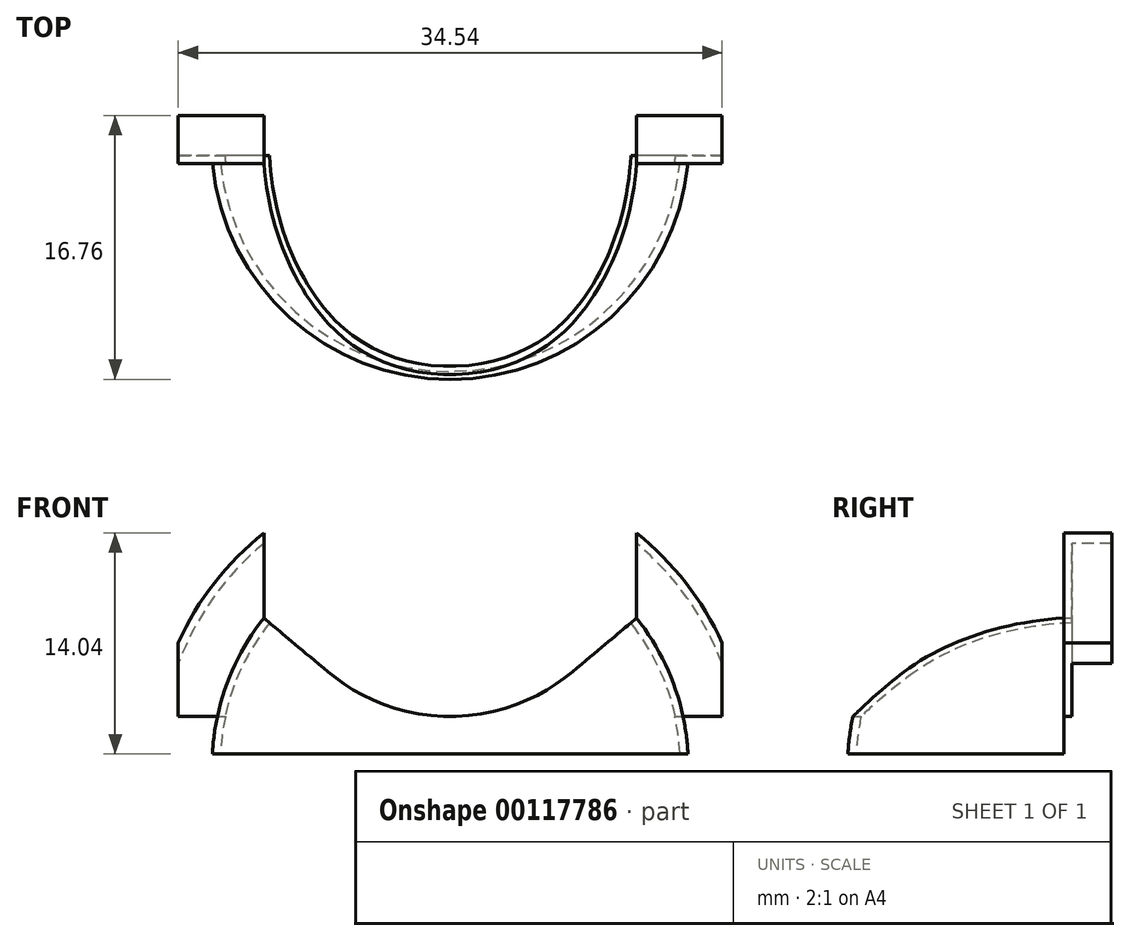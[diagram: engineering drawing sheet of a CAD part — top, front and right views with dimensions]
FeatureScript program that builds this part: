
annotation { "Feature Type Name" : "Feature", "Feature Type Description" : "" }
export const myFeature = defineFeature(function(context is Context, id is Id, definition is map)
    precondition{}
    {
        {
            var Q0;
            Q0=qCreatedBy(makeId("Right.planeOp"),FACE);
            var sketch = newSketch(context, id + "F0", { "sketchPlane" : qUnion([Q0])});
            skCircle(sketch, "E0", {"center": v(0, 0) * mm, "radius": 14.69 * mm});
            skLineSegment(sketch, "E1", {"start": v(1.59, 18.47) * mm, "end": v(-0.95, 18.47) * mm});
            skLineSegment(sketch, "E2", {"start": v(-0.95, 18.47) * mm, "end": v(-0.95, 14.66) * mm});
            skLineSegment(sketch, "E3", {"start": v(1.59, 18.47) * mm, "end": v(1.59, 18.97) * mm});
            skLineSegment(sketch, "E4", {"start": v(1.59, 18.97) * mm, "end": v(-1.46, 18.97) * mm});
            skLineSegment(sketch, "E5", {"start": v(-1.46, 18.97) * mm, "end": v(-1.46, 15.12) * mm});
            skCircle(sketch, "E6", {"center": v(0, 0) * mm, "radius": 15.2 * mm});
            skLineSegment(sketch, "E7", {"start": v(-15.2, 0) * mm, "end": v(-14.69, 0) * mm});
            skSolve(sketch);
        }
        {
            var Q0;
            {var subQ1=sQuery(id+"F0.wireOp",EDGE,"E1");Q0=makeQuery(id+"F0.imprint","IMPRINT",FACE,{"disambiguationData":[TD([[makeQuery(id+"F0.imprint","IMPRINT",EDGE,{"derivedFrom":subQ1}),-1.0]])]});}
            var Q1;
            {var subQ6=sQuery(id+"F0.wireOp",EDGE,"E7");Q1=makeQuery(id+"F0.imprint","IMPRINT",FACE,{"disambiguationData":[TD([[makeQuery(id+"F0.imprint","IMPRINT",EDGE,{"derivedFrom":subQ6}),1.0]])]});}
            var Q2;
            Q2=sQuery(id+"F0.wireOp",EDGE,"E7");
            revolve(context, id + "F1", {"entities" : qUnion([Q0, Q1]), "axis" : qUnion([Q2]), "revolveType" : RevolveType.SYMMETRIC, "angle" : 180 * degree});
        }
        {
            var Q0;
            Q0=qCreatedBy(makeId("Right.planeOp"),FACE);
            var sketch = newSketch(context, id + "F2", { "sketchPlane" : qUnion([Q0])});
            skLineSegment(sketch, "E8.bottom", {"start": v(1.59, 3.17) * mm, "end": v(-1.46, 3.17) * mm});
            skLineSegment(sketch, "E8.top", {"start": v(1.59, 0) * mm, "end": v(-1.46, 0) * mm});
            skLineSegment(sketch, "E8.left", {"start": v(1.59, 3.17) * mm, "end": v(1.59, 0) * mm});
            skLineSegment(sketch, "E8.right", {"start": v(-1.46, 3.17) * mm, "end": v(-1.46, 0) * mm});
            skSolve(sketch);
        }
        {
            var Q0;
            Q0=makeQuery(id+"F2.imprint","IMPRINT",FACE,{"disambiguationData":[TD([[makeQuery(id+"F2.imprint","IMPRINT",EDGE,{"derivedFrom":sQuery(id+"F2.wireOp",EDGE,"E8.bottom")}),1.0]])]});
            extrude(context, id + "F3", {"entities" : qUnion([Q0]), "operationType" : NewBodyOperationType.REMOVE, "endBound" : BoundingType.SYMMETRIC, "oppositeDirection" : true, "depth" : 50.8 * mm});
        }
        {
            var Q0;
            Q0=makeQuery(id+"F1.opRevolve","SWEPT_BODY",BODY,{"disambiguationData":[OSD([sQuery(id+"F0.wireOp",EDGE,"E0"),sQuery(id+"F0.wireOp",EDGE,"E1"),sQuery(id+"F0.wireOp",EDGE,"E2"),sQuery(id+"F0.wireOp",EDGE,"E3"),sQuery(id+"F0.wireOp",EDGE,"E4"),sQuery(id+"F0.wireOp",EDGE,"E5"),sQuery(id+"F0.wireOp",EDGE,"E6"),sQuery(id+"F0.wireOp",EDGE,"E7")])]});
            var Q1;
            Q1=makeQuery(id+"F3.boolean.opBoolean","COPY",EDGE,{"disambiguationData":[OD(1.0)],"derivedFrom":makeQuery(id+"F3.opExtrude","SWEPT_EDGE",EDGE,{"disambiguationData":[OSD([sQuery(id+"F2.wireOp",EDGE,"E8.top"),sQuery(id+"F2.wireOp",EDGE,"E8.right")])]})});
            transform(context, id + "F4", {"entities" : qUnion([Q0]), "transformType" : TransformType.COPY});
        }
        {
            var Q0;
            Q0=qCreatedBy(makeId("Front.planeOp"),FACE);
            var sketch = newSketch(context, id + "F5", { "sketchPlane" : qUnion([Q0])});
            skCircle(sketch, "E9", {"center": v(0, 15.24) * mm, "radius": 12.07 * mm});
            skLineSegment(sketch, "E10", {"start": v(11.83, 9.42) * mm, "end": v(7.76, 6) * mm});
            skLineSegment(sketch, "E11", {"start": v(-7.76, 6) * mm, "end": v(-11.83, 9.42) * mm});
            skLineSegment(sketch, "E12", {"start": v(-11.83, 9.42) * mm, "end": v(11.83, 9.42) * mm});
            skLineSegment(sketch, "E13", {"start": v(-11.83, 9.42) * mm, "end": v(-11.83, 20.56) * mm});
            skLineSegment(sketch, "E14", {"start": v(-11.83, 20.56) * mm, "end": v(11.83, 20.56) * mm});
            skLineSegment(sketch, "E15", {"start": v(11.83, 20.56) * mm, "end": v(11.83, 9.42) * mm});
            skSolve(sketch);
        }
        {
            var Q0;
            {var subQ0=sQuery(id+"F5.wireOp",EDGE,"1CEebHZN-BrZE-F3CF-ijxN-NzDrlZ3mt1Ko.top");Q0=makeQuery(id+"F5.imprint","IMPRINT",FACE,{"disambiguationData":[TD([[makeQuery(id+"F5.imprint","IMPRINT",EDGE,{"derivedFrom":subQ0}),-1.0]])]});}
            var Q1;
            {var subQ0=sQuery(id+"F5.wireOp",EDGE,"1CEebHZN-BrZE-F3CF-ijxN-NzDrlZ3mt1Ko.top");Q1=makeQuery(id+"F5.imprint","IMPRINT",FACE,{"disambiguationData":[TD([[makeQuery(id+"F5.imprint","IMPRINT",EDGE,{"derivedFrom":subQ0}),1.0]])]});}
            var Q2;
            Q2=makeQuery(id+"F5.imprint","IMPRINT",FACE,{"disambiguationData":[TD([[makeQuery(id+"F5.imprint","IMPRINT",EDGE,{"derivedFrom":sQuery(id+"F5.wireOp",EDGE,"1CEebHZN-BrZE-F3CF-ijxN-NzDrlZ3mt1Ko.bottom")}),-1.0]])]});
            var Q3;
            {var subQ1=sQuery(id+"F5.wireOp",EDGE,"E10");Q3=makeQuery(id+"F5.imprint","IMPRINT",FACE,{"disambiguationData":[TD([[makeQuery(id+"F5.imprint","IMPRINT",EDGE,{"derivedFrom":subQ1}),-1.0]])]});}
            var Q4;
            {var subQ0=sQuery(id+"F5.wireOp",EDGE,"E9");var subQ1=makeQuery(id+"F5.imprint","INTERSECT",VERTEX,{"derivedFrom":[subQ0,sQuery(id+"F5.wireOp",EDGE,"E10")]});Q4=makeQuery(id+"F5.imprint","IMPRINT",FACE,{"disambiguationData":[TD([[makeQuery(id+"F5.imprint","IMPRINT",EDGE,{"disambiguationData":[TD([[subQ1,1.0]])],"derivedFrom":subQ0}),1.0]])]});}
            var Q5;
            {var subQ0=sQuery(id+"F5.wireOp",EDGE,"E13");Q5=makeQuery(id+"F5.imprint","IMPRINT",FACE,{"disambiguationData":[TD([[makeQuery(id+"F5.imprint","IMPRINT",EDGE,{"derivedFrom":subQ0}),-1.0]])]});}
            var Q6;
            {var subQ0=sQuery(id+"F5.wireOp",EDGE,"E12");var subQ1=sQuery(id+"F5.wireOp",EDGE,"E9");var subQ2=makeQuery(id+"F5.imprint","INTERSECT",VERTEX,{"disambiguationData":[OD(0.0)],"derivedFrom":[subQ1,subQ0]});Q6=makeQuery(id+"F5.imprint","IMPRINT",FACE,{"disambiguationData":[TD([[makeQuery(id+"F5.imprint","IMPRINT",EDGE,{"disambiguationData":[TD([[subQ2,1.0]])],"derivedFrom":subQ1}),1.0]])]});}
            var Q7;
            {var subQ0=sQuery(id+"F5.wireOp",EDGE,"E11");Q7=makeQuery(id+"F5.imprint","IMPRINT",FACE,{"disambiguationData":[TD([[makeQuery(id+"F5.imprint","IMPRINT",EDGE,{"derivedFrom":subQ0}),-1.0]])]});}
            var Q8;
            {var subQ5=sQuery(id+"F5.wireOp",EDGE,"E15");Q8=makeQuery(id+"F5.imprint","IMPRINT",FACE,{"disambiguationData":[TD([[makeQuery(id+"F5.imprint","IMPRINT",EDGE,{"derivedFrom":subQ5}),-1.0]])]});}
            extrude(context, id + "F6", {"entities" : qUnion([Q0, Q1, Q2, Q3, Q4, Q5, Q6, Q7, Q8]), "operationType" : NewBodyOperationType.REMOVE, "endBound" : BoundingType.SYMMETRIC, "depth" : 50.8 * mm});
        }
        {
            var Q0;
            Q0=qCreatedBy(makeId("Front.planeOp"),FACE);
            var sketch = newSketch(context, id + "F7", { "sketchPlane" : qUnion([Q0])});
            skLineSegment(sketch, "E16.bottom", {"start": v(-17.27, 0) * mm, "end": v(-29.97, 0) * mm});
            skLineSegment(sketch, "E16.top", {"start": v(-17.27, 12.7) * mm, "end": v(-29.97, 12.7) * mm});
            skLineSegment(sketch, "E16.left", {"start": v(-17.27, 0) * mm, "end": v(-17.27, 12.7) * mm});
            skLineSegment(sketch, "E16.right", {"start": v(-29.97, 0) * mm, "end": v(-29.97, 12.7) * mm});
            skLineSegment(sketch, "E17.bottom", {"start": v(17.27, 0) * mm, "end": v(29.97, 0) * mm});
            skLineSegment(sketch, "E17.top", {"start": v(17.27, 12.7) * mm, "end": v(29.97, 12.7) * mm});
            skLineSegment(sketch, "E17.left", {"start": v(17.27, 0) * mm, "end": v(17.27, 12.7) * mm});
            skLineSegment(sketch, "E17.right", {"start": v(29.97, 0) * mm, "end": v(29.97, 12.7) * mm});
            skSolve(sketch);
        }
        {
            var Q0;
            Q0=makeQuery(id+"F7.imprint","IMPRINT",FACE,{"disambiguationData":[TD([[makeQuery(id+"F7.imprint","IMPRINT",EDGE,{"derivedFrom":sQuery(id+"F7.wireOp",EDGE,"E16.bottom")}),-1.0]])]});
            var Q1;
            Q1=makeQuery(id+"F7.imprint","IMPRINT",FACE,{"disambiguationData":[TD([[makeQuery(id+"F7.imprint","IMPRINT",EDGE,{"derivedFrom":sQuery(id+"F7.wireOp",EDGE,"E17.bottom")}),1.0]])]});
            extrude(context, id + "F8", {"entities" : qUnion([Q0, Q1]), "operationType" : NewBodyOperationType.REMOVE, "endBound" : BoundingType.SYMMETRIC, "depth" : 50.8 * mm});
        }
        {
            var Q0;
            Q0=qCreatedBy(makeId("Front.planeOp"),FACE);
            var sketch = newSketch(context, id + "F9", { "sketchPlane" : qUnion([Q0])});
            skLineSegment(sketch, "E18.bottom", {"start": v(-25.4, 0.8) * mm, "end": v(25.4, 0.8) * mm});
            skLineSegment(sketch, "E18.top", {"start": v(-25.4, -0.8) * mm, "end": v(25.4, -0.8) * mm});
            skLineSegment(sketch, "E18.left", {"start": v(-25.4, 0.8) * mm, "end": v(-25.4, -0.8) * mm});
            skLineSegment(sketch, "E18.right", {"start": v(25.4, 0.8) * mm, "end": v(25.4, -0.8) * mm});
            skPoint(sketch, "E18.middle", {"position": v(0, 0) * mm});
            skSolve(sketch);
        }
        {
            var Q0;
            Q0=makeQuery(id+"F9.imprint","IMPRINT",FACE,{"disambiguationData":[TD([[makeQuery(id+"F9.imprint","IMPRINT",EDGE,{"derivedFrom":sQuery(id+"F9.wireOp",EDGE,"E18.bottom")}),-1.0]])]});
            extrude(context, id + "F10", {"entities" : qUnion([Q0]), "operationType" : NewBodyOperationType.REMOVE, "depth" : 25.4 * mm});
        }
    });
